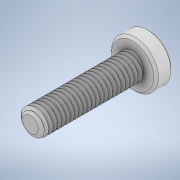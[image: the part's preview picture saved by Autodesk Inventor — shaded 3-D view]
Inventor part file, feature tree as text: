
AUTODESK INVENTOR PART (.ipt)
format: ipt  version: 2022 (Build 260153000, 153)  size: 439,808 bytes
history: mixed  units: mm
features: chamfer x1, imported_body x1
ambient origin geometry x8: Origin, YZ Plane, XZ Plane, XY Plane, X Axis, Y Axis, Z Axis, Center Point
bodies: Solid1 (imported_parasolid)
feature tree (2):
  chamfer  "Chamfer1"  [1 undecoded]
  imported_body  NMx_Import_Brep_tag  [imported B-rep: ~3 faces, bbox_mm=None]
note: 1 required parameter value undecoded (feature->parameter linkage not recoverable at this tier; creation-order binding heuristic only, values carry confidence <= 0.55)
